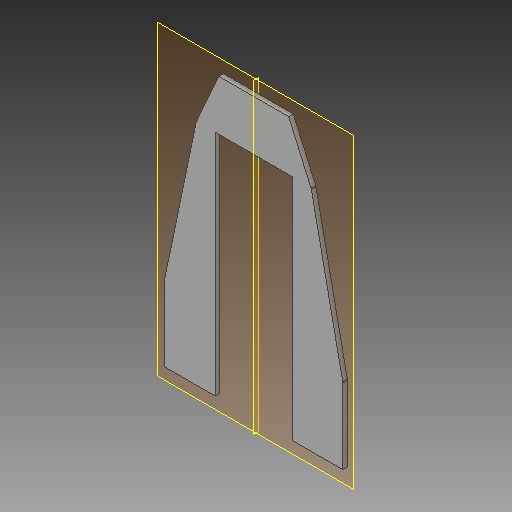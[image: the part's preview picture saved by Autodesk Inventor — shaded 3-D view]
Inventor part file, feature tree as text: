
AUTODESK INVENTOR PART (.ipt)
format: ipt  version: 2018 (Build 220112000, 112)  size: 242,688 bytes
history: native  units: mm
features: other x10, sheet_metal_op x3, sketch x3, plane x1, projected_geometry x1
ambient origin geometry x8: Origin, YZ Plane, XZ Plane, XY Plane, X Axis, Y Axis, Z Axis, Center Point
bodies: Solid1 (feature_tree)
feature tree (18):
  plane  "Work Plane1"
  sheet_metal_op  "Face1"
  other  "midtplan"
  other  "modplan parallel med plade"
  sheet_metal_op  "Face2"
  sketch  "Sketch1"  dims[d0=49.0mm]
  other  "Plate1"
  sketch  "Sketch2"  dims[d1=120.0mm]
  projected_geometry  "Projected Loop1"
  sketch  "Sketch4"  dims[d2=35.5mm d3=88.078826mm d4=44.039413mm d5=101.68943mm d6=50.844715mm d7=15.0mm d8=3.0mm d9=2.0mm d10=3.0mm d11=0.0mm d15=1.5mm d16=1.5mm d17=3.0mm d18=3.0mm d19=1.5mm d20=6.0mm d21=3.0mm]
  other  "Plate2"
  sheet_metal_op  "Bend1"
  other  "Cut1"
  other  "Definition1"
  parser-record x1  (decoder bookkeeping rows leaked as tree rows — omitted from the tree; the rows remain in map.json)
  other  "modul.iam"
  other  "stilladssøjle:1"
  other  "rør:1"
note: 1 file-system path scrubbed to <path> (originals preserved in map.json)
